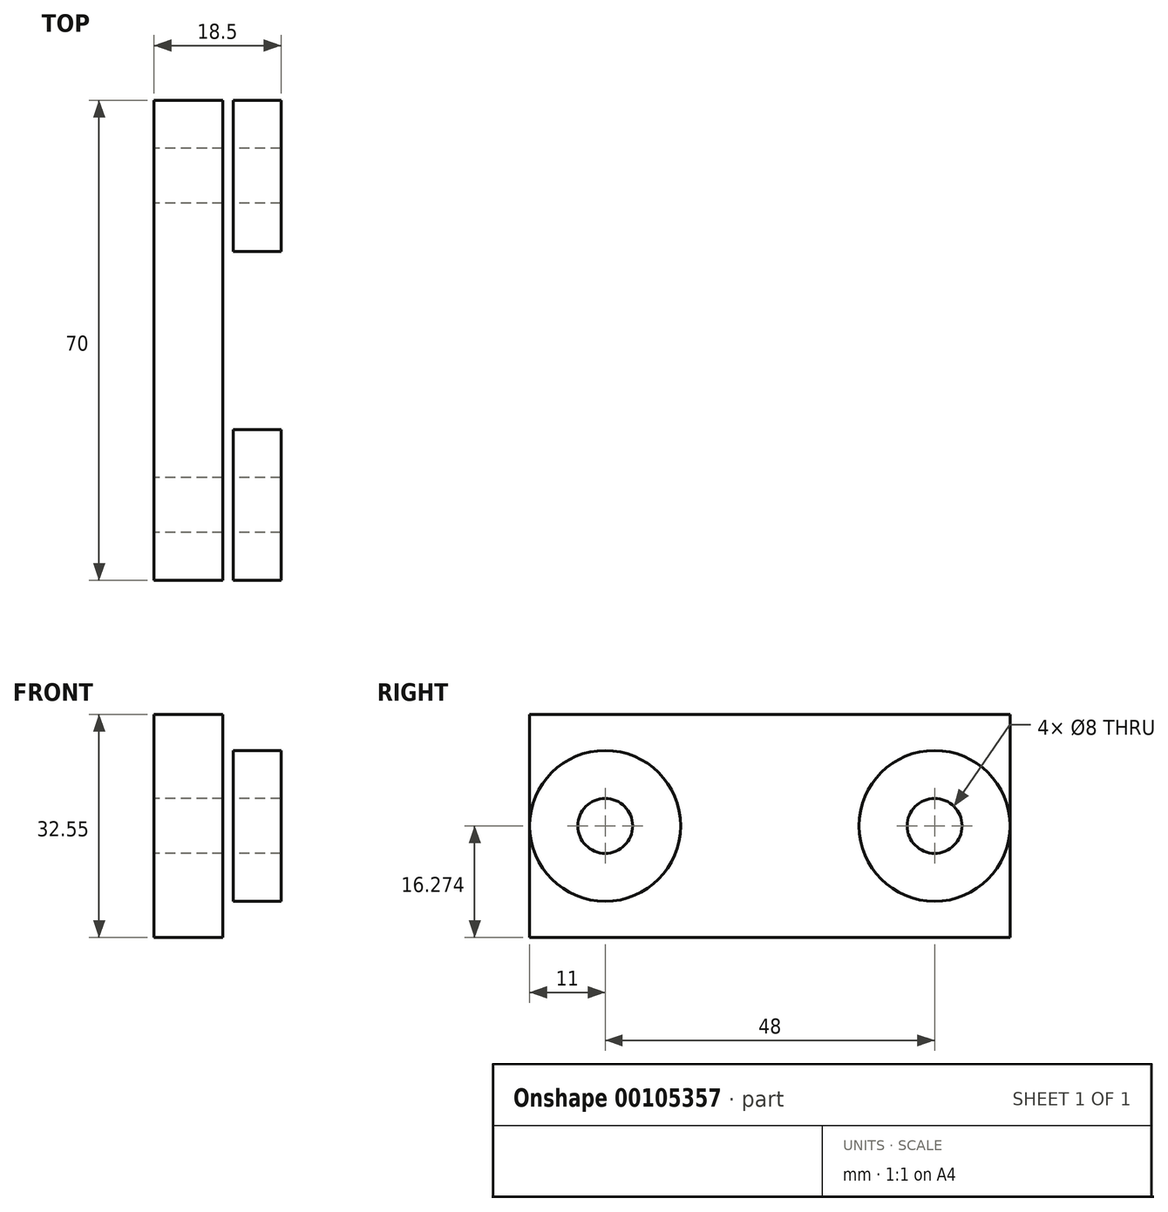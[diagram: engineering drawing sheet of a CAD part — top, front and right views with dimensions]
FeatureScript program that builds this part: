
annotation { "Feature Type Name" : "Feature", "Feature Type Description" : "" }
export const myFeature = defineFeature(function(context is Context, id is Id, definition is map)
    precondition{}
    {
        {
            var Q0;
            Q0=qCreatedBy(makeId("Front.planeOp"),FACE);
            var sketch = newSketch(context, id + "F0", { "sketchPlane" : qUnion([Q0])});
            skCircle(sketch, "E0", {"center": v(-10, 5.77) * mm, "radius": 10 * mm});
            skCircle(sketch, "E1", {"center": v(10, 5.77) * mm, "radius": 10 * mm});
            skCircle(sketch, "E2", {"center": v(0, 14.08) * mm, "radius": 3 * mm});
            skCircle(sketch, "E3", {"center": v(0, -11.55) * mm, "radius": 10 * mm});
            skCircle(sketch, "E4", {"center": v(12.2, -7.04) * mm, "radius": 3 * mm});
            skCircle(sketch, "E5", {"center": v(-12.2, -7.04) * mm, "radius": 3 * mm});
            skLineSegment(sketch, "E6.bottom", {"start": v(-3.5, 39.08) * mm, "end": v(3.5, 39.08) * mm});
            skLineSegment(sketch, "E6.top", {"start": v(-3.5, 17.08) * mm, "end": v(3.5, 17.08) * mm});
            skLineSegment(sketch, "E6.left", {"start": v(-3.5, 39.08) * mm, "end": v(-3.5, 17.08) * mm});
            skLineSegment(sketch, "E6.right", {"start": v(3.5, 39.08) * mm, "end": v(3.5, 17.08) * mm});
            skPoint(sketch, "E7", {"position": v(0, 17.08) * mm});
            skCircle(sketch, "E8", {"center": v(0, 0) * mm, "radius": 11.55 * mm, "construction": true});
            skLineSegment(sketch, "E9.1.0", {"start": v(-32.1, -22.57) * mm, "end": v(-13.04, -11.57) * mm});
            skLineSegment(sketch, "E9.1.1", {"start": v(-32.1, -22.57) * mm, "end": v(-35.6, -16.5) * mm});
            skLineSegment(sketch, "E9.1.2", {"start": v(-35.6, -16.5) * mm, "end": v(-16.54, -5.5) * mm});
            skLineSegment(sketch, "E9.1.3", {"start": v(-13.04, -11.57) * mm, "end": v(-16.54, -5.5) * mm});
            skLineSegment(sketch, "E9.2.0", {"start": v(35.6, -16.5) * mm, "end": v(16.54, -5.5) * mm});
            skLineSegment(sketch, "E9.2.1", {"start": v(35.6, -16.5) * mm, "end": v(32.1, -22.57) * mm});
            skLineSegment(sketch, "E9.2.2", {"start": v(32.1, -22.57) * mm, "end": v(13.04, -11.57) * mm});
            skLineSegment(sketch, "E9.2.3", {"start": v(16.54, -5.5) * mm, "end": v(13.04, -11.57) * mm});
            skLineSegment(sketch, "E10.bottom", {"start": v(-5, 17.08) * mm, "end": v(-15, 17.08) * mm});
            skLineSegment(sketch, "E10.top", {"start": v(-5, 49.63) * mm, "end": v(-15, 49.63) * mm});
            skLineSegment(sketch, "E10.left", {"start": v(-5, 17.08) * mm, "end": v(-5, 49.63) * mm});
            skLineSegment(sketch, "E10.right", {"start": v(-15, 17.08) * mm, "end": v(-15, 49.63) * mm});
            skSolve(sketch);
        }
        {
            var Q0;
            Q0=makeQuery(id+"F0.imprint","IMPRINT",FACE,{"disambiguationData":[TD([[makeQuery(id+"F0.imprint","IMPRINT",EDGE,{"derivedFrom":sQuery(id+"F0.wireOp",EDGE,"E10.bottom")}),-1.0]])]});
            extrude(context, id + "F1", {"entities" : qUnion([Q0]), "depth" : 70 * mm});
        }
        {
            var Q0;
            Q0=qCreatedBy(makeId("Right.planeOp"),FACE);
            var sketch = newSketch(context, id + "F2", { "sketchPlane" : qUnion([Q0])});
            skLineSegment(sketch, "E11.0", {"start": v(0, 17.08) * mm, "end": v(0, 49.63) * mm, "construction": true});
            skPoint(sketch, "E12", {"position": v(0, 33.35) * mm});
            skCircle(sketch, "E13", {"center": v(-11, 33.35) * mm, "radius": 11 * mm});
            skCircle(sketch, "E14", {"center": v(-59, 33.35) * mm, "radius": 11 * mm});
            skSolve(sketch);
        }
        {
            var Q0;
            Q0 = qSketchRegion(id + "F2", true);
            extrude(context, id + "F3", {"entities" : qUnion([Q0]), "endBound" : BoundingType.SYMMETRIC, "depth" : 7 * mm});
        }
        {
            var Q0;
            Q0=makeQuery(id+"F1.opExtrude","SWEPT_FACE",FACE,{"disambiguationData":[OSD([sQuery(id+"F0.wireOp",EDGE,"E10.right")])]});
            var sketch = newSketch(context, id + "F4", { "sketchPlane" : qUnion([Q0])});
            skCircle(sketch, "E15.0", {"center": v(59, 33.35) * mm, "radius": 11 * mm, "construction": true});
            skCircle(sketch, "E16.0", {"center": v(11, 33.35) * mm, "radius": 11 * mm, "construction": true});
            skCircle(sketch, "E17", {"center": v(11, 33.35) * mm, "radius": 4 * mm});
            skCircle(sketch, "E18", {"center": v(59, 33.35) * mm, "radius": 4 * mm});
            skSolve(sketch);
        }
        {
            var Q0;
            Q0 = qSketchRegion(id + "F4", true);
            extrude(context, id + "F5", {"entities" : qUnion([Q0]), "operationType" : NewBodyOperationType.REMOVE, "endBound" : BoundingType.THROUGH_ALL, "oppositeDirection" : true, "depth" : 25 * mm});
        }
    });
